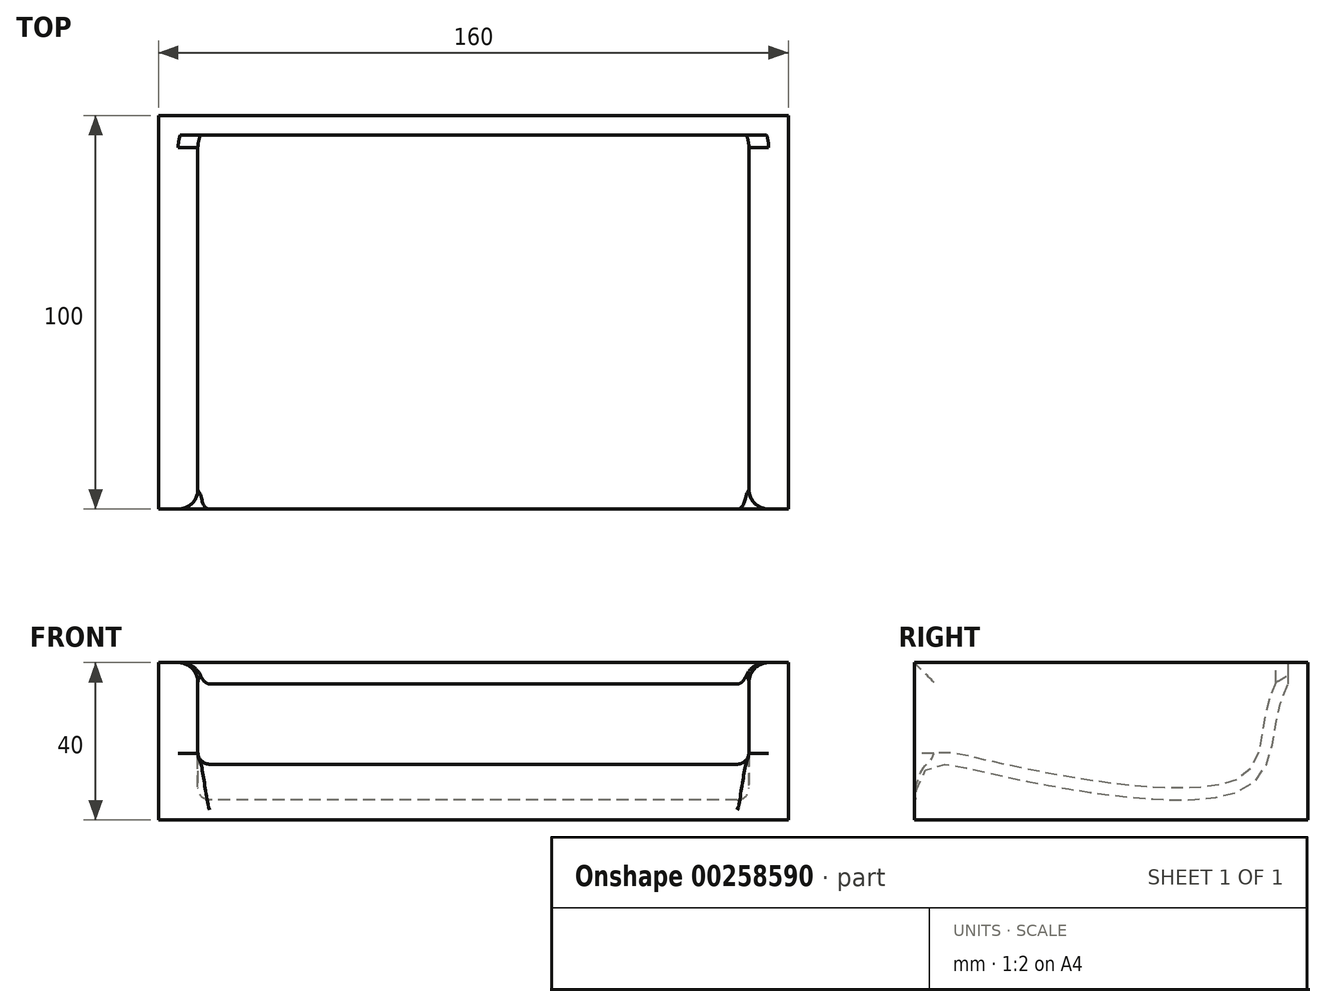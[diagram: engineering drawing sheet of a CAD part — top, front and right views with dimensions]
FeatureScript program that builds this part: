
annotation { "Feature Type Name" : "Feature", "Feature Type Description" : "" }
export const myFeature = defineFeature(function(context is Context, id is Id, definition is map)
    precondition{}
    {
        {
            var Q0;
            Q0=qCreatedBy(makeId("Top.planeOp"),FACE);
            var sketch = newSketch(context, id + "F0", { "sketchPlane" : qUnion([Q0])});
            skLineSegment(sketch, "E0.bottom", {"start": v(0, 0) * mm, "end": v(160, 0) * mm});
            skLineSegment(sketch, "E0.top", {"start": v(0, 100) * mm, "end": v(160, 100) * mm});
            skLineSegment(sketch, "E0.left", {"start": v(0, 0) * mm, "end": v(0, 100) * mm});
            skLineSegment(sketch, "E0.right", {"start": v(160, 0) * mm, "end": v(160, 100) * mm});
            skLineSegment(sketch, "E1.0", {"start": v(10, 95) * mm, "end": v(150, 95) * mm});
            skLineSegment(sketch, "E2.0", {"start": v(10, 0) * mm, "end": v(10, 95) * mm});
            skLineSegment(sketch, "E3.0", {"start": v(150, 0) * mm, "end": v(150, 95) * mm});
            skSolve(sketch);
        }
        {
            var Q0;
            Q0=makeQuery(id+"F0.imprint","IMPRINT",FACE,{"disambiguationData":[TD([[makeQuery(id+"F0.imprint","IMPRINT",EDGE,{"derivedFrom":sQuery(id+"F0.wireOp",EDGE,"E0.top")}),-1.0]])]});
            extrude(context, id + "F1", {"entities" : qUnion([Q0]), "depth" : 40 * mm});
        }
        {
            var Q0;
            Q0=makeQuery(id+"F1.opExtrude","SWEPT_FACE",FACE,{"disambiguationData":[OSD([sQuery(id+"F0.wireOp",EDGE,"E0.right")])]});
            var sketch = newSketch(context, id + "F2", { "sketchPlane" : qUnion([Q0])});
            skFitSpline(sketch, "E4", {"points": [v(0, 2.46) * mm, v(5.94, 14.1) * mm, v(20.78, 11.54) * mm, v(84.11, 8) * mm, v(92.3, 26.87) * mm, v(100, 40) * mm], "startDerivative": vector(11.41, 189.68) * mm, "endDerivative": vector(70.2, 36.89) * mm});
            skFitSpline(sketch, "E5.0", {"points": [v(-3, 2.64) * mm, v(-2.87, 4.71) * mm, v(-2.56, 7.36) * mm, v(-1.87, 10.19) * mm, v(-1.2, 12.02) * mm, v(-0.34, 13.6) * mm, v(0.75, 14.92) * mm, v(2.04, 15.94) * mm, v(3.41, 16.6) * mm, v(4.52, 16.9) * mm, v(5.35, 17.05) * mm, v(6.14, 17.14) * mm, v(7.15, 17.19) * mm, v(8.37, 17.15) * mm, v(9.61, 17.02) * mm, v(11.34, 16.75) * mm, v(13.68, 16.27) * mm, v(17.03, 15.48) * mm, v(20.43, 14.68) * mm, v(23.62, 13.97) * mm, v(27.1, 13.22) * mm, v(31.93, 12.24) * mm, v(38.27, 11.08) * mm, v(44.97, 10) * mm, v(51.82, 9.08) * mm, v(58.6, 8.42) * mm, v(65.1, 8.07) * mm, v(70.12, 8.1) * mm, v(73.76, 8.37) * mm, v(76.27, 8.68) * mm, v(78.54, 9.12) * mm, v(80.51, 9.67) * mm, v(82.17, 10.33) * mm, v(83.46, 11.07) * mm, v(84.5, 11.9) * mm, v(85.36, 12.83) * mm, v(86.07, 13.88) * mm, v(86.88, 15.46) * mm, v(87.65, 17.8) * mm, v(88.18, 20.52) * mm, v(88.55, 22.85) * mm, v(88.84, 24.64) * mm, v(89.15, 26.47) * mm, v(89.54, 28.33) * mm, v(90.02, 30.14) * mm, v(90.76, 32.48) * mm, v(91.9, 35.25) * mm, v(93.63, 38.24) * mm, v(95.8, 40.8) * mm, v(97.61, 42.13) * mm, v(98.6, 42.66) * mm]});
            skSolve(sketch);
        }
        {
            var Q0;
            {var subQ0=sQuery(id+"F2.wireOp",EDGE,"E4");Q0=makeQuery(id+"F2.imprint","IMPRINT",FACE,{"disambiguationData":[TD([[makeQuery(id+"F2.imprint","IMPRINT",EDGE,{"derivedFrom":subQ0}),-1.0]])]});}
            extrude(context, id + "F3", {"entities" : qUnion([Q0]), "operationType" : NewBodyOperationType.ADD, "oppositeDirection" : true, "depth" : 160 * mm});
        }
        {
            var Q0;
            {var subQ0=sQuery(id+"F2.wireOp",EDGE,"E4");var subQ1=sQuery(id+"F0.wireOp",EDGE,"E0.right");Q0=makeQuery(id+"F3.boolean.opBoolean","INTERSECT",EDGE,{"derivedFrom":[makeQuery(id+"F1.opExtrude","SWEPT_FACE",FACE,{"disambiguationData":[OSD([sQuery(id+"F0.wireOp",EDGE,"E2.0")])]}),makeQuery(id+"F3.opExtrude","SWEPT_FACE",FACE,{"disambiguationData":[OSD([subQ0]),TDD([makeQuery(id+"F2.imprint","IMPRINT",EDGE,{"disambiguationData":[TD([[makeQuery(id+"F2.imprint","INTERSECT",VERTEX,{"disambiguationData":[OD(0.0)],"derivedFrom":[makeQuery(id+"F1.opExtrude","CAP_EDGE",EDGE,{"disambiguationData":[OSD([subQ1])],"isStart":false}),subQ0]}),1.0]])],"derivedFrom":subQ0})])]})]});}
            var Q1;
            {var subQ0=sQuery(id+"F2.wireOp",EDGE,"E4");var subQ1=sQuery(id+"F0.wireOp",EDGE,"E0.right");Q1=makeQuery(id+"F3.boolean.opBoolean","INTERSECT",EDGE,{"derivedFrom":[makeQuery(id+"F1.opExtrude","SWEPT_FACE",FACE,{"disambiguationData":[OSD([sQuery(id+"F0.wireOp",EDGE,"E3.0")])]}),makeQuery(id+"F3.opExtrude","SWEPT_FACE",FACE,{"disambiguationData":[OSD([subQ0]),TDD([makeQuery(id+"F2.imprint","IMPRINT",EDGE,{"disambiguationData":[TD([[makeQuery(id+"F2.imprint","INTERSECT",VERTEX,{"disambiguationData":[OD(0.0)],"derivedFrom":[makeQuery(id+"F1.opExtrude","CAP_EDGE",EDGE,{"disambiguationData":[OSD([subQ1])],"isStart":false}),subQ0]}),1.0]])],"derivedFrom":subQ0})])]})]});}
            fillet(context, id + "F4", {"entities" : qUnion([Q0, Q1]), "radius" : 3 * mm, "tangentPropagation" : true, "allowEdgeOverflow" : false});
        }
        {
            var Q0;
            {var subQ0=sQuery(id+"F2.wireOp",EDGE,"E4");Q0=makeQuery(id+"F2.imprint","IMPRINT",FACE,{"disambiguationData":[TD([[makeQuery(id+"F2.imprint","IMPRINT",EDGE,{"derivedFrom":subQ0}),1.0]])]});}
            extrude(context, id + "F5", {"entities" : qUnion([Q0]), "operationType" : NewBodyOperationType.ADD, "oppositeDirection" : true, "depth" : 5 * mm});
        }
        {
            var Q0;
            Q0=makeQuery(id+"F1.opExtrude","CAP_EDGE",EDGE,{"disambiguationData":[OSD([sQuery(id+"F0.wireOp",EDGE,"E2.0")])],"isStart":false});
            var Q1;
            Q1=makeQuery(id+"F1.opExtrude","CAP_EDGE",EDGE,{"disambiguationData":[OSD([sQuery(id+"F0.wireOp",EDGE,"E3.0")])],"isStart":false});
            var Q2;
            Q2=makeQuery(id+"F1.opExtrude","SWEPT_EDGE",EDGE,{"disambiguationData":[OSD([sQuery(id+"F0.wireOp",EDGE,"E0.bottom"),sQuery(id+"F0.wireOp",EDGE,"E2.0")])]});
            fillet(context, id + "F6", {"entities" : qUnion([Q0, Q1, Q2]), "radius" : 5 * mm, "tangentPropagation" : true, "allowEdgeOverflow" : false});
        }
    });
